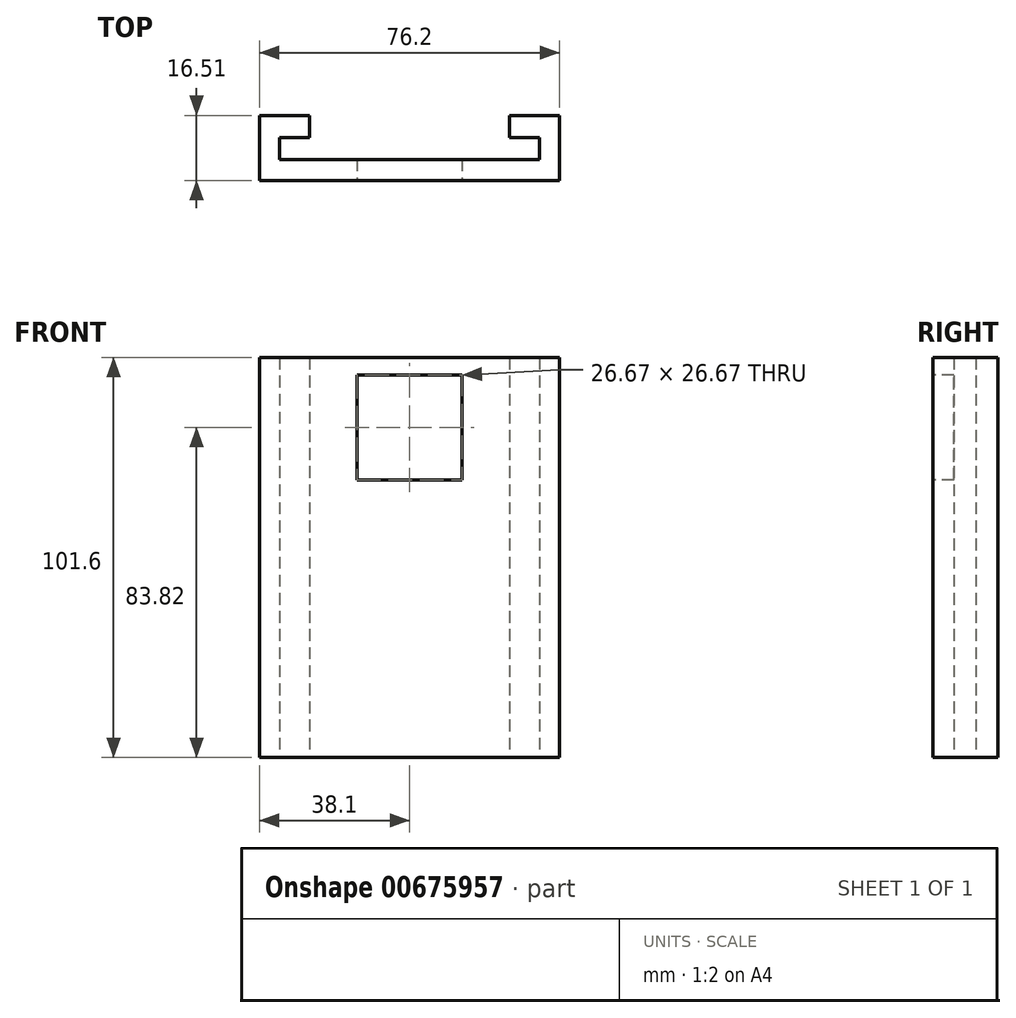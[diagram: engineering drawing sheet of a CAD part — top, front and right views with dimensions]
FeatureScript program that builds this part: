
annotation { "Feature Type Name" : "Feature", "Feature Type Description" : "" }
export const myFeature = defineFeature(function(context is Context, id is Id, definition is map)
    precondition{}
    {
        {
            var Q0;
            Q0=qCreatedBy(makeId("Top.planeOp"),FACE);
            var sketch = newSketch(context, id + "F0", { "sketchPlane" : qUnion([Q0])});
            skLineSegment(sketch, "E0", {"start": v(-38.1, -5.33) * mm, "end": v(0, -5.33) * mm});
            skLineSegment(sketch, "E1", {"start": v(-38.1, 11.18) * mm, "end": v(-38.1, -5.33) * mm});
            skLineSegment(sketch, "E2", {"start": v(-38.1, 11.18) * mm, "end": v(-25.4, 11.18) * mm});
            skLineSegment(sketch, "E3", {"start": v(-25.4, 11.18) * mm, "end": v(-25.4, 5.59) * mm});
            skLineSegment(sketch, "E4", {"start": v(-25.4, 5.59) * mm, "end": v(-33.02, 5.59) * mm});
            skLineSegment(sketch, "E5", {"start": v(-33.02, 5.59) * mm, "end": v(-33.02, 0) * mm});
            skLineSegment(sketch, "E6", {"start": v(-33.02, 0) * mm, "end": v(0, 0) * mm});
            skLineSegment(sketch, "E7.MirrorCS", {"start": v(25.4, 11.18) * mm, "end": v(25.4, 5.59) * mm});
            skLineSegment(sketch, "E8.MirrorCS", {"start": v(33.02, 0) * mm, "end": v(0, 0) * mm});
            skLineSegment(sketch, "E9.MirrorCS", {"start": v(38.1, -5.33) * mm, "end": v(0, -5.33) * mm});
            skLineSegment(sketch, "E10.MirrorCS", {"start": v(33.02, 5.59) * mm, "end": v(33.02, 0) * mm});
            skLineSegment(sketch, "E11.MirrorCS", {"start": v(38.1, 11.18) * mm, "end": v(25.4, 11.18) * mm});
            skLineSegment(sketch, "E12.MirrorCS", {"start": v(25.4, 5.59) * mm, "end": v(33.02, 5.59) * mm});
            skLineSegment(sketch, "E13.MirrorCS", {"start": v(38.1, 11.18) * mm, "end": v(38.1, -5.33) * mm});
            skSolve(sketch);
        }
        {
            var Q0;
            Q0=makeQuery(id+"F0.imprint","IMPRINT",FACE,{"disambiguationData":[TD([[makeQuery(id+"F0.imprint","IMPRINT",EDGE,{"derivedFrom":sQuery(id+"F0.wireOp",EDGE,"E0")}),1.0]])]});
            extrude(context, id + "F1", {"entities" : qUnion([Q0]), "endBound" : BoundingType.SYMMETRIC, "depth" : 101.6 * mm, "offsetDistance" : 25.4 * mm});
        }
        {
            var Q0;
            Q0=makeQuery(id+"F1.opExtrude","SWEPT_FACE",FACE,{"disambiguationData":[OSD([sQuery(id+"F0.wireOp",EDGE,"E0"),sQuery(id+"F0.wireOp",EDGE,"E9.MirrorCS")])]});
            var sketch = newSketch(context, id + "F2", { "sketchPlane" : qUnion([Q0])});
            skLineSegment(sketch, "E14.bottom", {"start": v(13.33, 19.69) * mm, "end": v(-13.34, 19.69) * mm});
            skLineSegment(sketch, "E14.top", {"start": v(13.33, 46.36) * mm, "end": v(-13.34, 46.36) * mm});
            skLineSegment(sketch, "E14.left", {"start": v(13.33, 19.69) * mm, "end": v(13.33, 46.36) * mm});
            skLineSegment(sketch, "E14.right", {"start": v(-13.34, 19.69) * mm, "end": v(-13.34, 46.36) * mm});
            skPoint(sketch, "E14.middle", {"position": v(0, 33.02) * mm});
            skSolve(sketch);
        }
        {
            var Q0;
            Q0=makeQuery(id+"F2.imprint","IMPRINT",FACE,{"disambiguationData":[TD([[makeQuery(id+"F2.imprint","IMPRINT",EDGE,{"derivedFrom":sQuery(id+"F2.wireOp",EDGE,"E14.bottom")}),-1.0]])]});
            extrude(context, id + "F3", {"entities" : qUnion([Q0]), "operationType" : NewBodyOperationType.REMOVE, "endBound" : BoundingType.THROUGH_ALL, "oppositeDirection" : true, "depth" : 25.4 * mm, "offsetDistance" : 25.4 * mm});
        }
    });
